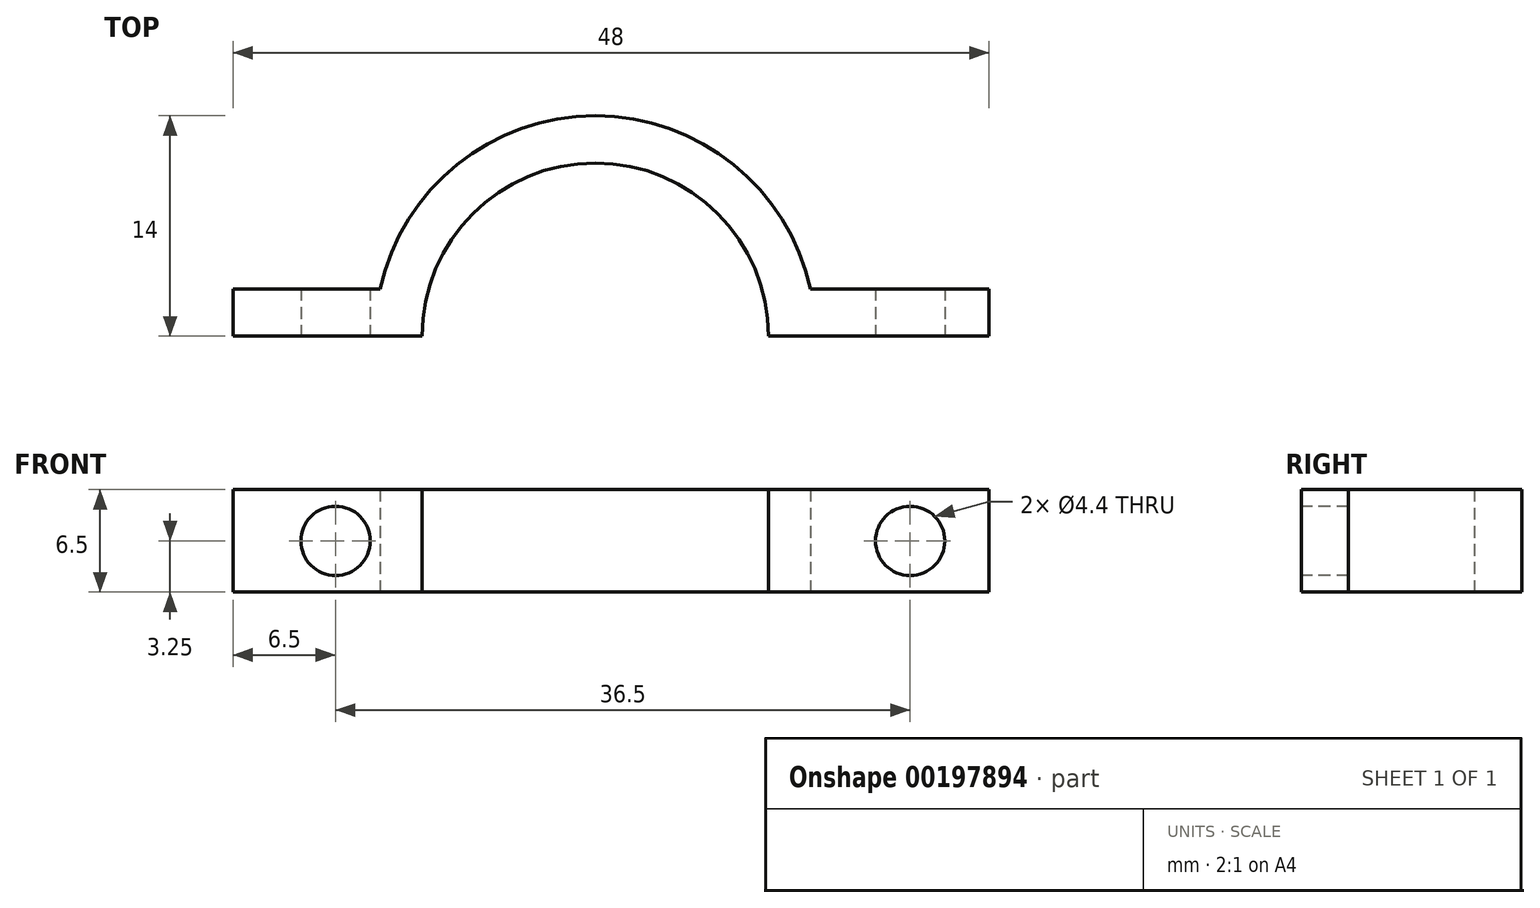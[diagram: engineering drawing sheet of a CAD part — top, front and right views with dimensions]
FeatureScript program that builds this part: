
annotation { "Feature Type Name" : "Feature", "Feature Type Description" : "" }
export const myFeature = defineFeature(function(context is Context, id is Id, definition is map)
    precondition{}
    {
        {
            var Q0;
            Q0=qCreatedBy(makeId("Top.planeOp"),FACE);
            var sketch = newSketch(context, id + "F0", { "sketchPlane" : qUnion([Q0])});
            skLineSegment(sketch, "E0", {"start": v(11, 0) * mm, "end": v(23, 0) * mm});
            skLineSegment(sketch, "E1", {"start": v(0, 0) * mm, "end": v(0, 12.38) * mm, "construction": true});
            skPoint(sketch, "E1.endSnap0", {"position": v(0, 10.5) * mm});
            skArc(sketch, "E2", {"start": v(11, 0) * mm, "mid": v(7.78, 7.78) * mm, "end": v(0, 11) * mm});
            skLineSegment(sketch, "E3", {"start": v(0, 0) * mm, "end": v(-12.3, 0) * mm, "construction": true});
            skArc(sketch, "E4.0", {"start": v(13.67, 3) * mm, "mid": v(8.77, 10.9) * mm, "end": v(0, 14) * mm});
            skLineSegment(sketch, "E4.1", {"start": v(13.67, 3) * mm, "end": v(23, 3) * mm});
            skArc(sketch, "E5.MirrorCS", {"start": v(-11, 0) * mm, "mid": v(-7.78, 7.78) * mm, "end": v(0, 11) * mm});
            skArc(sketch, "E6.MirrorCS", {"start": v(-13.67, 3) * mm, "mid": v(-8.77, 10.9) * mm, "end": v(0, 14) * mm});
            skLineSegment(sketch, "E7.MirrorCS", {"start": v(-13.67, 3) * mm, "end": v(-23, 3) * mm});
            skLineSegment(sketch, "E8.MirrorCS", {"start": v(-11, 0) * mm, "end": v(-23, 0) * mm});
            skLineSegment(sketch, "E9.MirrorCS", {"start": v(-23, 0) * mm, "end": v(-23, 3) * mm});
            skLineSegment(sketch, "E10.bottom", {"start": v(23, 3) * mm, "end": v(25, 3) * mm});
            skLineSegment(sketch, "E10.top", {"start": v(23, 0) * mm, "end": v(25, 0) * mm});
            skLineSegment(sketch, "E10.right", {"start": v(25, 3) * mm, "end": v(25, 0) * mm});
            skSolve(sketch);
        }
        {
            var Q0;
            Q0=makeQuery(id+"F0.imprint","IMPRINT",FACE,{"disambiguationData":[TD([[makeQuery(id+"F0.imprint","IMPRINT",EDGE,{"derivedFrom":sQuery(id+"F0.wireOp",EDGE,"E0")}),1.0]])]});
            extrude(context, id + "F1", {"entities" : qUnion([Q0]), "depth" : 6.5 * mm});
        }
        {
            var Q0;
            Q0=makeQuery(id+"F1.opExtrude","SWEPT_FACE",FACE,{"disambiguationData":[OSD([sQuery(id+"F0.wireOp",EDGE,"E8.MirrorCS")])]});
            var sketch = newSketch(context, id + "F2", { "sketchPlane" : qUnion([Q0])});
            skLineSegment(sketch, "E11", {"start": v(0, 0) * mm, "end": v(0, 3.25) * mm, "construction": true});
            skLineSegment(sketch, "E12", {"start": v(0, 3.25) * mm, "end": v(-16.5, 3.25) * mm, "construction": true});
            skLineSegment(sketch, "E13", {"start": v(0, 3.25) * mm, "end": v(20, 3.25) * mm, "construction": true});
            skCircle(sketch, "E14", {"center": v(-16.5, 3.25) * mm, "radius": 2.2 * mm});
            skCircle(sketch, "E15", {"center": v(20, 3.25) * mm, "radius": 2.2 * mm});
            skSolve(sketch);
        }
        {
            var Q0;
            Q0 = qSketchRegion(id + "F2", true);
            extrude(context, id + "F3", {"entities" : qUnion([Q0]), "operationType" : NewBodyOperationType.REMOVE, "oppositeDirection" : true, "depth" : 25 * mm});
        }
    });
